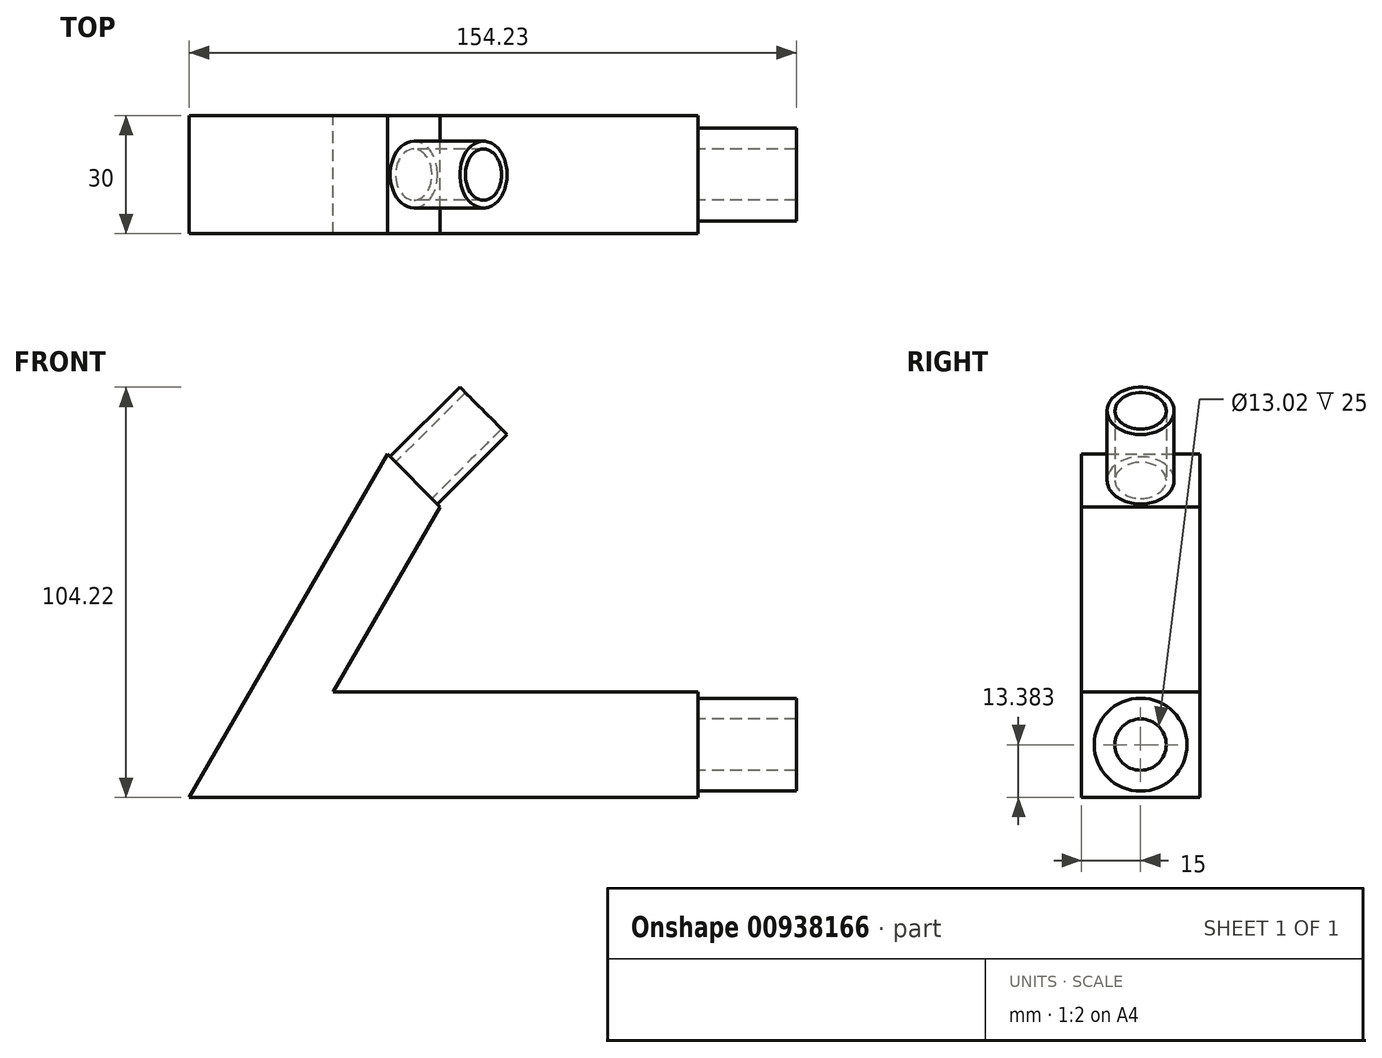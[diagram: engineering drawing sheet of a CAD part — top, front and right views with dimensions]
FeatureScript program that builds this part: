
annotation { "Feature Type Name" : "Feature", "Feature Type Description" : "" }
export const myFeature = defineFeature(function(context is Context, id is Id, definition is map)
    precondition{}
    {
        {
            var Q0;
            Q0=qCreatedBy(makeId("Front.planeOp"),FACE);
            var sketch = newSketch(context, id + "F0", { "sketchPlane" : qUnion([Q0])});
            skLineSegment(sketch, "E0", {"start": v(-15.75, 58.47) * mm, "end": v(-66.12, -28.78) * mm});
            skLineSegment(sketch, "E1", {"start": v(-66.12, -28.78) * mm, "end": v(63.1, -28.78) * mm});
            skLineSegment(sketch, "E2", {"start": v(63.1, -28.78) * mm, "end": v(63.1, -2.01) * mm});
            skLineSegment(sketch, "E3", {"start": v(63.1, -2.01) * mm, "end": v(-29.53, -2.01) * mm});
            skLineSegment(sketch, "E4", {"start": v(-29.53, -2.01) * mm, "end": v(-2.35, 45.05) * mm});
            skLineSegment(sketch, "E5", {"start": v(-15.75, 58.47) * mm, "end": v(-2.35, 45.05) * mm});
            skSolve(sketch);
        }
        {
            var Q0;
            Q0=makeQuery(id+"F0.imprint","IMPRINT",FACE,{"disambiguationData":[TD([[makeQuery(id+"F0.imprint","IMPRINT",EDGE,{"derivedFrom":sQuery(id+"F0.wireOp",EDGE,"E0")}),1.0]])]});
            extrude(context, id + "F1", {"entities" : qUnion([Q0]), "depth" : 30 * mm, "offsetDistance" : 25 * mm});
        }
        {
            var Q0;
            Q0=makeQuery(id+"F1.opExtrude","SWEPT_FACE",FACE,{"disambiguationData":[OSD([sQuery(id+"F0.wireOp",EDGE,"E5")])]});
            var sketch = newSketch(context, id + "F2", { "sketchPlane" : qUnion([Q0])});
            skLineSegment(sketch, "E6", {"start": v(-30, 52.5) * mm, "end": v(0, 33.54) * mm, "construction": true});
            skLineSegment(sketch, "E7", {"start": v(0, 33.54) * mm, "end": v(0, 52.5) * mm, "construction": true});
            skLineSegment(sketch, "E8", {"start": v(0, 52.5) * mm, "end": v(-30, 33.54) * mm, "construction": true});
            skCircle(sketch, "E9", {"center": v(-15, 43.02) * mm, "radius": 6.5 * mm});
            skCircle(sketch, "E10", {"center": v(-15, 43.02) * mm, "radius": 8.5 * mm});
            skSolve(sketch);
        }
        {
            var Q0;
            Q0 = qSketchRegion(id + "F2", true);
            extrude(context, id + "F3", {"entities" : qUnion([Q0]), "operationType" : NewBodyOperationType.ADD, "depth" : 25 * mm, "offsetDistance" : 25 * mm});
        }
        {
            var Q0;
            Q0=makeQuery(id+"F1.opExtrude","SWEPT_FACE",FACE,{"disambiguationData":[OSD([sQuery(id+"F0.wireOp",EDGE,"E2")])]});
            var sketch = newSketch(context, id + "F4", { "sketchPlane" : qUnion([Q0])});
            skLineSegment(sketch, "E11", {"start": v(-30, -2.01) * mm, "end": v(0, -28.78) * mm, "construction": true});
            skLineSegment(sketch, "E12", {"start": v(0, -28.78) * mm, "end": v(0, -2.01) * mm, "construction": true});
            skLineSegment(sketch, "E13", {"start": v(0, -2.01) * mm, "end": v(-30, -28.78) * mm, "construction": true});
            skCircle(sketch, "E14", {"center": v(-15, -15.4) * mm, "radius": 6.5 * mm});
            skCircle(sketch, "E15", {"center": v(-15, -15.4) * mm, "radius": 11.8 * mm});
            skSolve(sketch);
        }
        {
            var Q0;
            Q0=makeQuery(id+"F4.imprint","IMPRINT",FACE,{"disambiguationData":[TD([[makeQuery(id+"F4.imprint","IMPRINT",EDGE,{"derivedFrom":sQuery(id+"F4.wireOp",EDGE,"E14")}),-1.0]])]});
            extrude(context, id + "F5", {"entities" : qUnion([Q0]), "operationType" : NewBodyOperationType.ADD, "depth" : 25 * mm, "offsetDistance" : 25 * mm});
        }
    });
